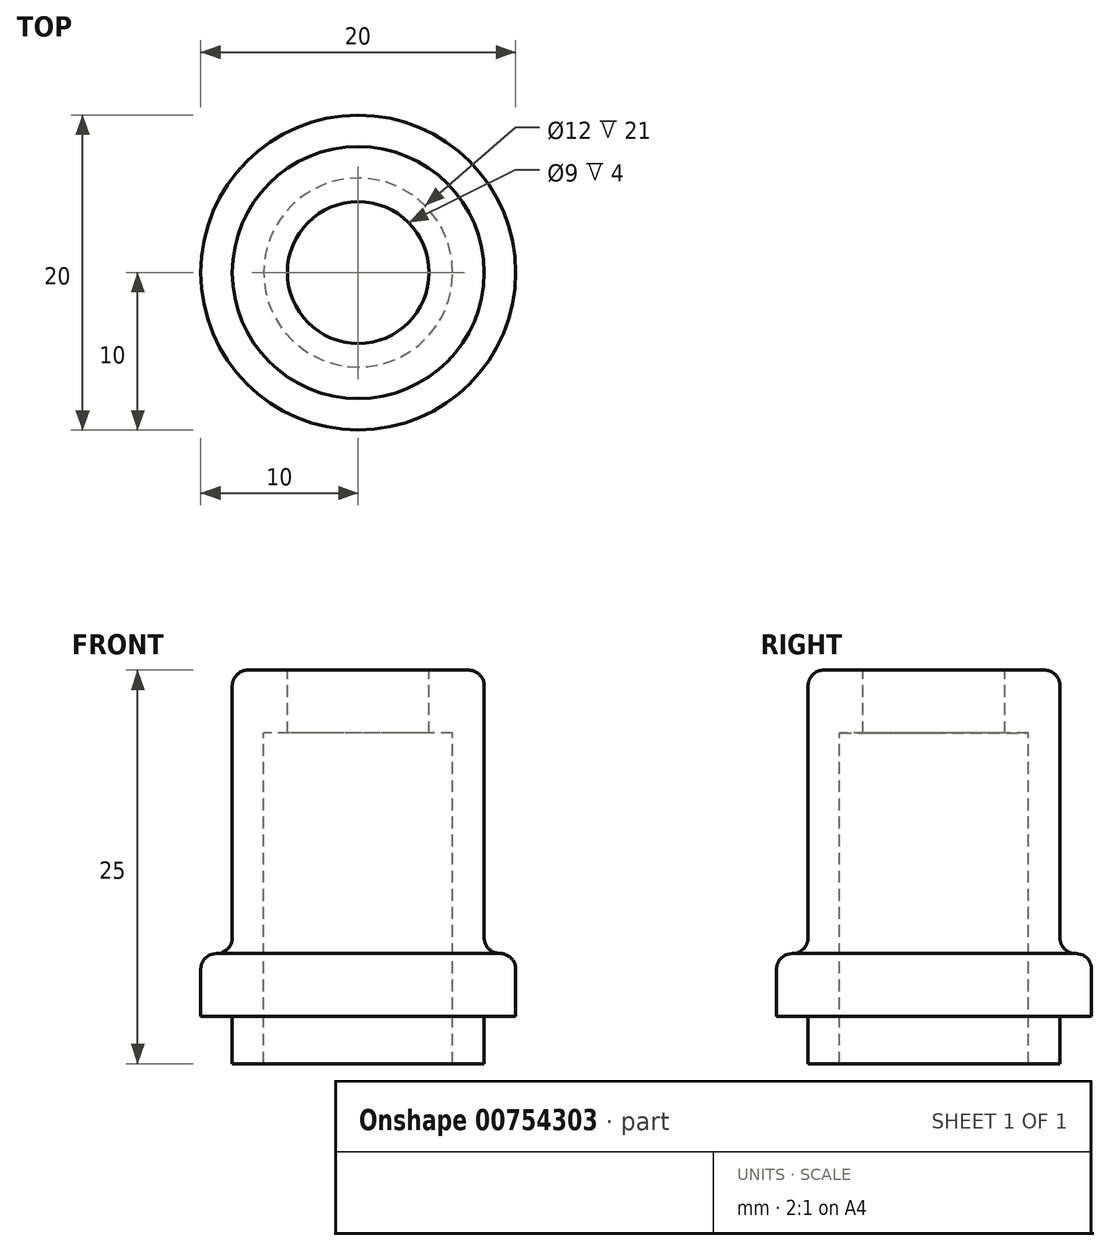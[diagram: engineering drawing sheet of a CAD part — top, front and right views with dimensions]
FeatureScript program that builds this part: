
annotation { "Feature Type Name" : "Feature", "Feature Type Description" : "" }
export const myFeature = defineFeature(function(context is Context, id is Id, definition is map)
    precondition{}
    {
        {
            var Q0;
            Q0=qCreatedBy(makeId("Top.planeOp"),FACE);
            var sketch = newSketch(context, id + "F0", { "sketchPlane" : qUnion([Q0])});
            skCircle(sketch, "E0", {"center": v(0, 0) * mm, "radius": 8 * mm});
            skCircle(sketch, "E1", {"center": v(0, 0) * mm, "radius": 10 * mm});
            skCircle(sketch, "E2", {"center": v(0, 0) * mm, "radius": 6 * mm});
            skSolve(sketch);
        }
        {
            var Q0;
            Q0=makeQuery(id+"F0.imprint","IMPRINT",FACE,{"disambiguationData":[TD([[makeQuery(id+"F0.imprint","IMPRINT",EDGE,{"derivedFrom":sQuery(id+"F0.wireOp",EDGE,"E0")}),1.0]])]});
            extrude(context, id + "F1", {"entities" : qUnion([Q0]), "oppositeDirection" : true, "depth" : 3 * mm, "offsetDistance" : 25 * mm});
        }
        {
            var Q0;
            Q0=makeQuery(id+"F0.imprint","IMPRINT",FACE,{"disambiguationData":[TD([[makeQuery(id+"F0.imprint","IMPRINT",EDGE,{"derivedFrom":sQuery(id+"F0.wireOp",EDGE,"E0")}),-1.0]])]});
            var Q1;
            Q1=makeQuery(id+"F0.imprint","IMPRINT",FACE,{"disambiguationData":[TD([[makeQuery(id+"F0.imprint","IMPRINT",EDGE,{"derivedFrom":sQuery(id+"F0.wireOp",EDGE,"E0")}),1.0]])]});
            extrude(context, id + "F2", {"entities" : qUnion([Q0, Q1]), "operationType" : NewBodyOperationType.ADD, "depth" : 4 * mm, "offsetDistance" : 25 * mm});
        }
        {
            var Q0;
            Q0=makeQuery(id+"F1.opExtrude","CAP_FACE",FACE,{"disambiguationData":[OSD([sQuery(id+"F0.wireOp",EDGE,"E0"),sQuery(id+"F0.wireOp",EDGE,"E2")])],"isStart":false});
            extrude(context, id + "F3", {"entities" : qUnion([Q0]), "operationType" : NewBodyOperationType.ADD, "oppositeDirection" : true, "depth" : 25 * mm, "offsetDistance" : 25 * mm});
        }
        {
            var Q0;
            Q0=makeQuery(id+"F0.imprint","IMPRINT",FACE,{"disambiguationData":[TD([[makeQuery(id+"F0.imprint","IMPRINT",EDGE,{"derivedFrom":sQuery(id+"F0.wireOp",EDGE,"E2")}),1.0]])]});
            extrude(context, id + "F4", {"entities" : qUnion([Q0]), "operationType" : NewBodyOperationType.ADD, "depth" : 22 * mm, "offsetDistance" : 25 * mm, "hasSecondDirection" : true, "secondDirectionOppositeDirection" : false, "secondDirectionDepth" : 18 * mm});
        }
        {
            var Q0;
            Q0=makeQuery(id+"F3.boolean.opBoolean","INTERSECT",EDGE,{"derivedFrom":[makeQuery(id+"F2.opExtrude","CAP_FACE",FACE,{"disambiguationData":[OSD([sQuery(id+"F0.wireOp",EDGE,"E1"),sQuery(id+"F0.wireOp",EDGE,"E2")])],"isStart":false}),makeQuery(id+"F3.opExtrude","SWEPT_FACE",FACE,{"disambiguationData":[OSD([sQuery(id+"F0.wireOp",EDGE,"E0")])]})]});
            var Q1;
            Q1=makeQuery(id+"F2.opExtrude","CAP_EDGE",EDGE,{"disambiguationData":[OSD([sQuery(id+"F0.wireOp",EDGE,"E1")])],"isStart":false});
            var Q2;
            Q2=makeQuery(id+"F3.opExtrude","CAP_EDGE",EDGE,{"disambiguationData":[OSD([sQuery(id+"F0.wireOp",EDGE,"E0")])],"isStart":false});
            fillet(context, id + "F5", {"entities" : qUnion([Q0, Q1, Q2]), "radius" : 1 * mm, "tangentPropagation" : true, "allowEdgeOverflow" : false});
        }
        {
            var Q0;
            {var subQ0=sQuery(id+"F0.wireOp",EDGE,"E2");Q0=makeQuery(id+"F4.boolean.opBoolean","MERGE",FACE,{"derivedFrom":[makeQuery(id+"F3.opExtrude","CAP_FACE",FACE,{"disambiguationData":[OSD([sQuery(id+"F0.wireOp",EDGE,"E0"),subQ0])],"isStart":false}),makeQuery(id+"F4.opExtrude","CAP_FACE",FACE,{"disambiguationData":[OSD([subQ0])],"isStart":false})]});}
            var sketch = newSketch(context, id + "F6", { "sketchPlane" : qUnion([Q0])});
            skCircle(sketch, "E3", {"center": v(0, 0) * mm, "radius": 4.5 * mm});
            skSolve(sketch);
        }
        {
            var Q0;
            Q0 = qSketchRegion(id + "F6", true);
            extrude(context, id + "F7", {"entities" : qUnion([Q0]), "operationType" : NewBodyOperationType.REMOVE, "oppositeDirection" : true, "depth" : 25 * mm, "offsetDistance" : 25 * mm, "hasSecondDirection" : true, "secondDirectionOppositeDirection" : false, "secondDirectionDepth" : 25 * mm});
        }
    });
